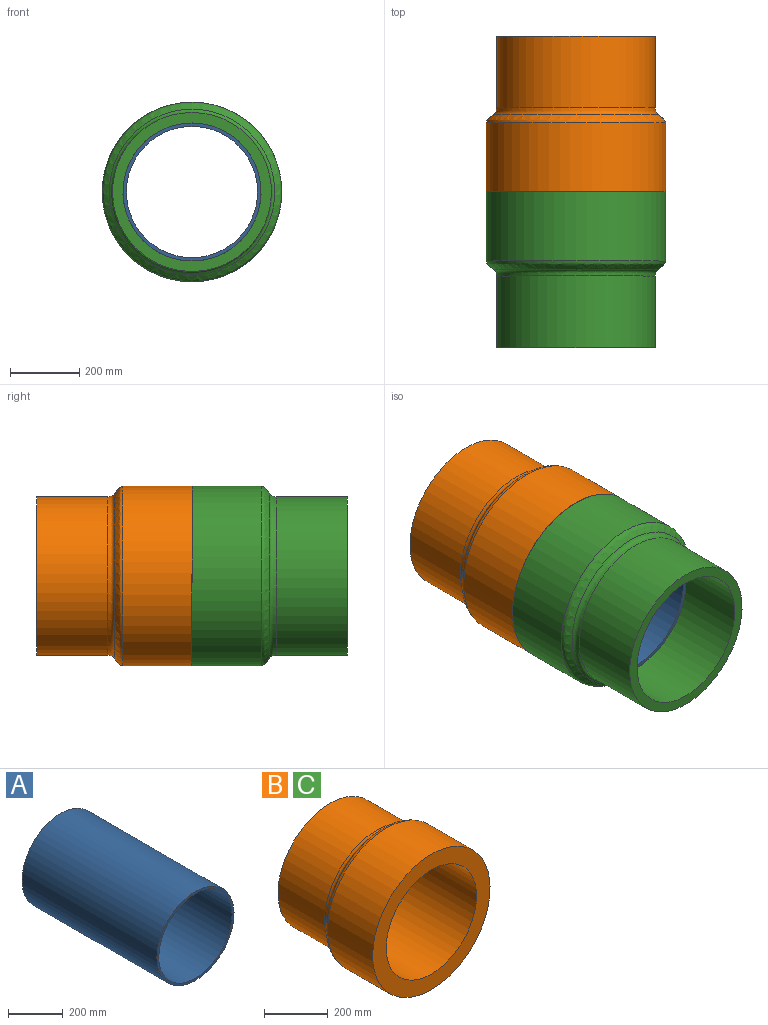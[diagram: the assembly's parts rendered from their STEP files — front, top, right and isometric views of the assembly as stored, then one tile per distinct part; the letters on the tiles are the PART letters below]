
ASSEMBLY  parts=3 mates=2
PART A: 4 faces, bbox 400x700x400 mm
  f0: cylinder r=190mm len=700mm, axis (0,1,0), area 835663.6mm2, adj f2,f3
  f1: cylinder r=200mm len=700mm, axis (0,1,0), area 879645.9mm2, adj f2,f3
  f2: plane 400x400mm, normal (0,-1,0), area 12252.2mm2, adj f0,f1
  f3: plane 400x400mm, normal (0,1,0), area 12252.2mm2, adj f0,f1
PART B: 7 faces, bbox 520x450x520 mm
  f0: plane 520x520mm, normal (0,-1,0), area 86708mm2, adj f1,f6
  f1: cylinder r=200mm len=450mm, axis (0,-1,0), area 565486.7mm2, adj f0,f2
  f2: plane 460x460mm, normal (0,1,0), area 40526.5mm2, adj f1,f3
  f3: cylinder r=230mm len=460mm, axis (0,-1,0), area 298439.7mm2, adj f2,f4
  f4: revolved ~479.33x479.33mm, area 34615.1mm2, adj f3,f5
  f5: revolved ~520x520mm, area 50830.7mm2, adj f4,f6
  f6: cylinder r=260mm len=520mm, axis (0,-1,0), area 326725.6mm2, adj f0,f5
PART C: same geometry as B
PLACE A rot(axis=(1,-0.03,0.03),0deg) t=(75.31,-658.03,8.23)mm fixed
PLACE B rot(axis=(1,-0.03,0.03),0deg) t=(75.31,-884.55,25.71)mm fixed
PLACE C rot(axis=(-1,0,0),180deg) t=(75.31,-1331.52,-9.25)mm
MATE revolute C.f1 <-> A.f1  axis (0,1,0) through (75.31,-1108.03,8.23)mm
MATE revolute B.f1 <-> A.f1  axis (0,-1,0) through (75.31,-883.03,8.23)mm
